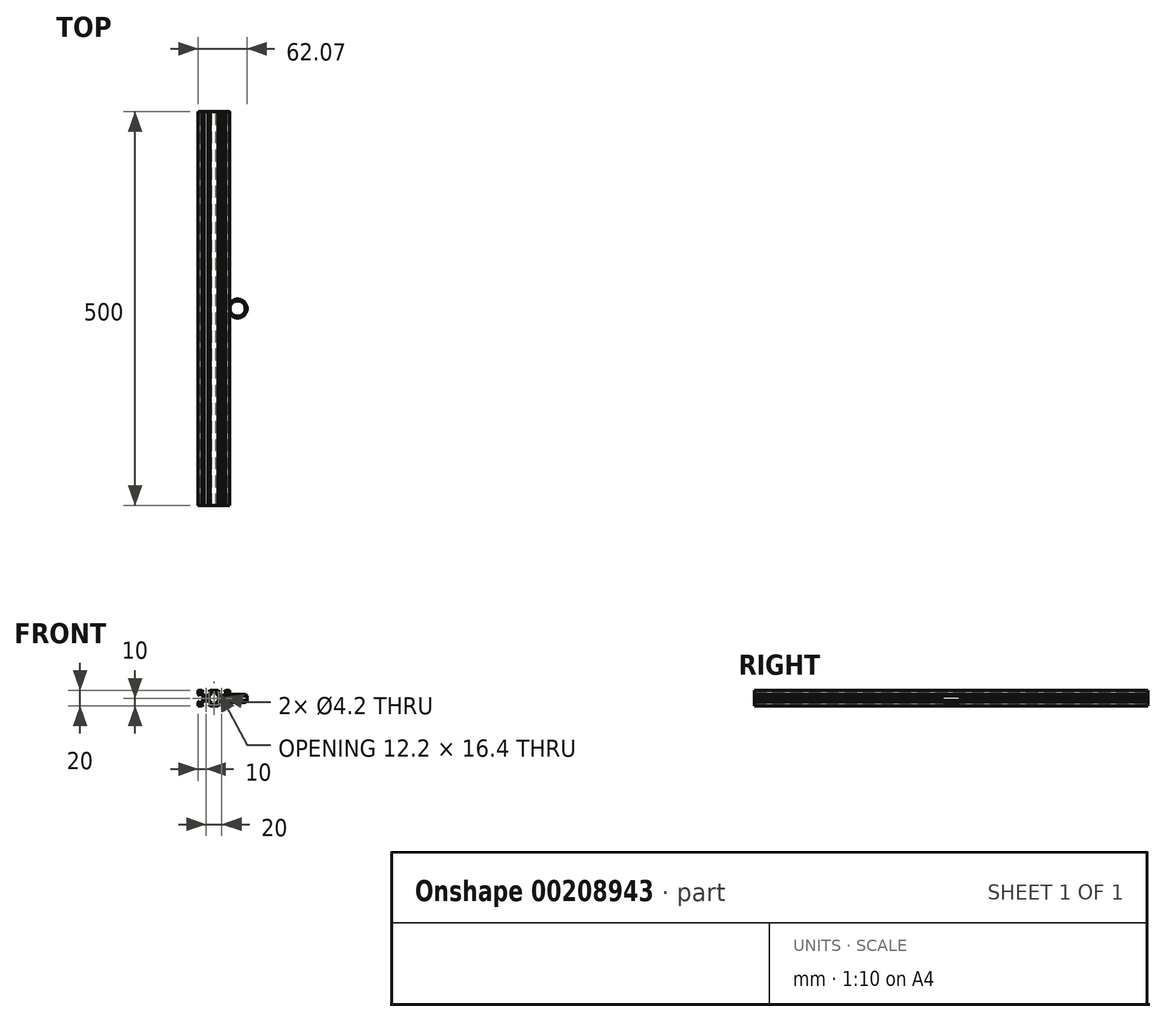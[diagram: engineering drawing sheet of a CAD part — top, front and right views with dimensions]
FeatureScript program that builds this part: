
annotation { "Feature Type Name" : "Feature", "Feature Type Description" : "" }
export const myFeature = defineFeature(function(context is Context, id is Id, definition is map)
    precondition{}
    {
        {
            var Q0;
            Q0=qCreatedBy(makeId("Front.planeOp"),FACE);
            var sketch = newSketch(context, id + "F0", { "sketchPlane" : qUnion([Q0])});
            skLineSegment(sketch, "E0", {"start": v(2.7, -8.2) * mm, "end": v(2.7, -6.24) * mm});
            skLineSegment(sketch, "E1", {"start": v(2.7, -6.24) * mm, "end": v(6.1, -2.84) * mm});
            skLineSegment(sketch, "E2", {"start": v(6.1, -2.84) * mm, "end": v(6.1, 2.84) * mm});
            skLineSegment(sketch, "E3", {"start": v(6.1, 2.84) * mm, "end": v(2.7, 6.24) * mm});
            skLineSegment(sketch, "E4", {"start": v(2.7, 6.24) * mm, "end": v(2.7, 8.2) * mm});
            skLineSegment(sketch, "E5", {"start": v(2.7, 8.2) * mm, "end": v(0, 8.2) * mm});
            skLineSegment(sketch, "E6", {"start": v(0, 8.2) * mm, "end": v(0, 0) * mm});
            skLineSegment(sketch, "E7", {"start": v(2.7, -8.2) * mm, "end": v(0, -8.2) * mm});
            skLineSegment(sketch, "E8", {"start": v(0, -8.2) * mm, "end": v(0, 0) * mm});
            skPoint(sketch, "E9.middle", {"position": v(0, 0) * mm});
            skLineSegment(sketch, "E10", {"start": v(5.07, 10) * mm, "end": v(0, 10) * mm});
            skLineSegment(sketch, "E11", {"start": v(0, 10) * mm, "end": v(0, 8.2) * mm});
            skLineSegment(sketch, "E12", {"start": v(0, -10) * mm, "end": v(0, -8.2) * mm});
            skPoint(sketch, "E13.endSnap0", {"position": v(6.1, 0) * mm});
            skLineSegment(sketch, "E14", {"start": v(0, -10) * mm, "end": v(5.07, -10) * mm});
            skCircle(sketch, "E15", {"center": v(10, 0) * mm, "radius": 2.1 * mm});
            skLineSegment(sketch, "E16", {"start": v(5.07, 10) * mm, "end": v(6.87, 8.2) * mm});
            skLineSegment(sketch, "E17", {"start": v(6.87, 8.2) * mm, "end": v(4.5, 8.2) * mm});
            skLineSegment(sketch, "E18", {"start": v(4.5, 8.2) * mm, "end": v(4.5, 6.56) * mm});
            skLineSegment(sketch, "E19", {"start": v(4.5, 6.56) * mm, "end": v(7.53, 3.53) * mm});
            skPoint(sketch, "E20.endSnap0", {"position": v(9.63, 5.16) * mm});
            skLineSegment(sketch, "E21", {"start": v(7.53, 3.53) * mm, "end": v(10, 3.53) * mm});
            skLineSegment(sketch, "E22.MirrorCS", {"start": v(12.47, 3.53) * mm, "end": v(10, 3.53) * mm});
            skLineSegment(sketch, "E23.MirrorCS", {"start": v(15.5, 6.56) * mm, "end": v(12.47, 3.53) * mm});
            skLineSegment(sketch, "E24.MirrorCS", {"start": v(15.5, 8.2) * mm, "end": v(15.5, 6.56) * mm});
            skLineSegment(sketch, "E25.MirrorCS", {"start": v(13.13, 8.2) * mm, "end": v(15.5, 8.2) * mm});
            skLineSegment(sketch, "E26.MirrorCS", {"start": v(14.93, 10) * mm, "end": v(13.13, 8.2) * mm});
            skLineSegment(sketch, "E27.MirrorCS", {"start": v(14.93, 10) * mm, "end": v(19.5, 10) * mm});
            skLineSegment(sketch, "E28.MirrorCS", {"start": v(20, 4.93) * mm, "end": v(18.2, 3.12) * mm});
            skLineSegment(sketch, "E29.MirrorCS", {"start": v(18.2, 5.5) * mm, "end": v(16.56, 5.5) * mm});
            skLineSegment(sketch, "E30.MirrorCS", {"start": v(16.56, 5.5) * mm, "end": v(13.53, 2.47) * mm});
            skLineSegment(sketch, "E31.MirrorCS", {"start": v(13.53, -2.47) * mm, "end": v(13.53, 0) * mm});
            skLineSegment(sketch, "E32.MirrorCS", {"start": v(13.53, 2.47) * mm, "end": v(13.53, 0) * mm});
            skLineSegment(sketch, "E33.MirrorCS", {"start": v(18.2, 3.12) * mm, "end": v(18.2, 5.5) * mm});
            skLineSegment(sketch, "E34.MirrorCS", {"start": v(16.56, -5.5) * mm, "end": v(13.53, -2.47) * mm});
            skLineSegment(sketch, "E35.MirrorCS", {"start": v(18.2, -5.5) * mm, "end": v(16.56, -5.5) * mm});
            skLineSegment(sketch, "E36.MirrorCS", {"start": v(18.2, -3.13) * mm, "end": v(18.2, -5.5) * mm});
            skLineSegment(sketch, "E37.MirrorCS", {"start": v(20, -4.93) * mm, "end": v(18.2, -3.12) * mm});
            skLineSegment(sketch, "E38", {"start": v(20, 9.5) * mm, "end": v(20, 4.93) * mm});
            skLineSegment(sketch, "E39.MirrorCS", {"start": v(20, -9.5) * mm, "end": v(20, -4.93) * mm});
            skLineSegment(sketch, "E40.MirrorCS", {"start": v(14.93, -10) * mm, "end": v(19.5, -10) * mm});
            skLineSegment(sketch, "E41.MirrorCS", {"start": v(14.93, -10) * mm, "end": v(13.13, -8.2) * mm});
            skLineSegment(sketch, "E42.MirrorCS", {"start": v(13.13, -8.2) * mm, "end": v(15.5, -8.2) * mm});
            skLineSegment(sketch, "E43.MirrorCS", {"start": v(15.5, -8.2) * mm, "end": v(15.5, -6.56) * mm});
            skLineSegment(sketch, "E44.MirrorCS", {"start": v(15.5, -6.56) * mm, "end": v(12.47, -3.53) * mm});
            skLineSegment(sketch, "E45.MirrorCS", {"start": v(12.47, -3.53) * mm, "end": v(10, -3.53) * mm});
            skLineSegment(sketch, "E46.MirrorCS", {"start": v(7.53, -3.53) * mm, "end": v(10, -3.53) * mm});
            skLineSegment(sketch, "E47.MirrorCS", {"start": v(4.5, -6.56) * mm, "end": v(7.53, -3.53) * mm});
            skLineSegment(sketch, "E48.MirrorCS", {"start": v(4.5, -8.2) * mm, "end": v(4.5, -6.56) * mm});
            skLineSegment(sketch, "E49.MirrorCS", {"start": v(6.87, -8.2) * mm, "end": v(4.5, -8.2) * mm});
            skLineSegment(sketch, "E50.MirrorCS", {"start": v(5.07, -10) * mm, "end": v(6.87, -8.2) * mm});
            skLineSegment(sketch, "E51.MirrorCS", {"start": v(-7.53, 3.53) * mm, "end": v(-10, 3.53) * mm});
            skCircle(sketch, "E52.MirrorC", {"center": v(-10, 0) * mm, "radius": 2.1 * mm});
            skLineSegment(sketch, "E53.MirrorCS", {"start": v(-6.1, -2.84) * mm, "end": v(-6.1, 2.84) * mm});
            skLineSegment(sketch, "E54.MirrorCS", {"start": v(-18.2, -3.13) * mm, "end": v(-18.2, -5.5) * mm});
            skLineSegment(sketch, "E55.MirrorCS", {"start": v(-14.93, 10) * mm, "end": v(-19.5, 10) * mm});
            skLineSegment(sketch, "E56.MirrorCS", {"start": v(0, -10) * mm, "end": v(-5.07, -10) * mm});
            skLineSegment(sketch, "E57.MirrorCS", {"start": v(-14.93, -10) * mm, "end": v(-13.13, -8.2) * mm});
            skLineSegment(sketch, "E58.MirrorCS", {"start": v(-14.93, 10) * mm, "end": v(-13.13, 8.2) * mm});
            skLineSegment(sketch, "E59.MirrorCS", {"start": v(-6.87, 8.2) * mm, "end": v(-4.5, 8.2) * mm});
            skLineSegment(sketch, "E60.MirrorCS", {"start": v(-20, -4.93) * mm, "end": v(-18.2, -3.12) * mm});
            skLineSegment(sketch, "E61.MirrorCS", {"start": v(-2.7, -8.2) * mm, "end": v(0, -8.2) * mm});
            skLineSegment(sketch, "E62.MirrorCS", {"start": v(-20, 4.93) * mm, "end": v(-18.2, 3.12) * mm});
            skLineSegment(sketch, "E63.MirrorCS", {"start": v(-2.7, -8.2) * mm, "end": v(-2.7, -6.24) * mm});
            skLineSegment(sketch, "E64.MirrorCS", {"start": v(-7.53, -3.53) * mm, "end": v(-10, -3.53) * mm});
            skLineSegment(sketch, "E65.MirrorCS", {"start": v(-13.13, -8.2) * mm, "end": v(-15.5, -8.2) * mm});
            skLineSegment(sketch, "E66.MirrorCS", {"start": v(-14.93, -10) * mm, "end": v(-19.5, -10) * mm});
            skLineSegment(sketch, "E67.MirrorCS", {"start": v(-6.87, -8.2) * mm, "end": v(-4.5, -8.2) * mm});
            skLineSegment(sketch, "E68.MirrorCS", {"start": v(-5.07, 10) * mm, "end": v(-6.87, 8.2) * mm});
            skLineSegment(sketch, "E69.MirrorCS", {"start": v(-13.53, 2.47) * mm, "end": v(-13.53, 0) * mm});
            skPoint(sketch, "E70.MirrorP", {"position": v(-6.1, 0) * mm});
            skLineSegment(sketch, "E71.MirrorCS", {"start": v(-15.5, -8.2) * mm, "end": v(-15.5, -6.56) * mm});
            skLineSegment(sketch, "E72.MirrorCS", {"start": v(-5.07, 10) * mm, "end": v(0, 10) * mm});
            skLineSegment(sketch, "E73.MirrorCS", {"start": v(-20, 9.5) * mm, "end": v(-20, 4.93) * mm});
            skLineSegment(sketch, "E74.MirrorCS", {"start": v(-18.2, 5.5) * mm, "end": v(-16.56, 5.5) * mm});
            skLineSegment(sketch, "E75.MirrorCS", {"start": v(-18.2, 3.12) * mm, "end": v(-18.2, 5.5) * mm});
            skLineSegment(sketch, "E76.MirrorCS", {"start": v(-15.5, 8.2) * mm, "end": v(-15.5, 6.56) * mm});
            skLineSegment(sketch, "E77.MirrorCS", {"start": v(-2.7, 6.24) * mm, "end": v(-2.7, 8.2) * mm});
            skLineSegment(sketch, "E78.MirrorCS", {"start": v(-16.56, 5.5) * mm, "end": v(-13.53, 2.47) * mm});
            skLineSegment(sketch, "E79.MirrorCS", {"start": v(-15.5, 6.56) * mm, "end": v(-12.47, 3.53) * mm});
            skLineSegment(sketch, "E80.MirrorCS", {"start": v(-16.56, -5.5) * mm, "end": v(-13.53, -2.47) * mm});
            skLineSegment(sketch, "E81.MirrorCS", {"start": v(-4.5, 6.56) * mm, "end": v(-7.53, 3.53) * mm});
            skLineSegment(sketch, "E82.MirrorCS", {"start": v(-20, -9.5) * mm, "end": v(-20, -4.93) * mm});
            skLineSegment(sketch, "E83.MirrorCS", {"start": v(-2.7, -6.24) * mm, "end": v(-6.1, -2.84) * mm});
            skLineSegment(sketch, "E84.MirrorCS", {"start": v(-4.5, 8.2) * mm, "end": v(-4.5, 6.56) * mm});
            skLineSegment(sketch, "E85.MirrorCS", {"start": v(-18.2, -5.5) * mm, "end": v(-16.56, -5.5) * mm});
            skLineSegment(sketch, "E86.MirrorCS", {"start": v(-4.5, -8.2) * mm, "end": v(-4.5, -6.56) * mm});
            skLineSegment(sketch, "E87.MirrorCS", {"start": v(-12.47, 3.53) * mm, "end": v(-10, 3.53) * mm});
            skLineSegment(sketch, "E88.MirrorCS", {"start": v(-13.53, -2.47) * mm, "end": v(-13.53, 0) * mm});
            skLineSegment(sketch, "E89.MirrorCS", {"start": v(-6.1, 2.84) * mm, "end": v(-2.7, 6.24) * mm});
            skLineSegment(sketch, "E90.MirrorCS", {"start": v(-15.5, -6.56) * mm, "end": v(-12.47, -3.53) * mm});
            skLineSegment(sketch, "E91.MirrorCS", {"start": v(-2.7, 8.2) * mm, "end": v(0, 8.2) * mm});
            skLineSegment(sketch, "E92.MirrorCS", {"start": v(-5.07, -10) * mm, "end": v(-6.87, -8.2) * mm});
            skLineSegment(sketch, "E93.MirrorCS", {"start": v(-4.5, -6.56) * mm, "end": v(-7.53, -3.53) * mm});
            skLineSegment(sketch, "E94.MirrorCS", {"start": v(-12.47, -3.53) * mm, "end": v(-10, -3.53) * mm});
            skLineSegment(sketch, "E95.MirrorCS", {"start": v(-13.13, 8.2) * mm, "end": v(-15.5, 8.2) * mm});
            skPoint(sketch, "E96.MirrorP", {"position": v(-9.63, 5.16) * mm});
            skPoint(sketch, "E97.visualSharp", {"position": v(20, 10) * mm});
            skArc(sketch, "E97.filletArc", {"start": v(20, 9.5) * mm, "mid": v(19.85, 9.85) * mm, "end": v(19.5, 10) * mm});
            skPoint(sketch, "E98.visualSharp", {"position": v(20, -10) * mm});
            skArc(sketch, "E98.filletArc", {"start": v(19.5, -10) * mm, "mid": v(19.85, -9.85) * mm, "end": v(20, -9.5) * mm});
            skPoint(sketch, "E99.visualSharp", {"position": v(-20, -10) * mm});
            skArc(sketch, "E99.filletArc", {"start": v(-20, -9.5) * mm, "mid": v(-19.85, -9.85) * mm, "end": v(-19.5, -10) * mm});
            skPoint(sketch, "E100.visualSharp", {"position": v(-20, 10) * mm});
            skArc(sketch, "E100.filletArc", {"start": v(-19.5, 10) * mm, "mid": v(-19.85, 9.85) * mm, "end": v(-20, 9.5) * mm});
            skSolve(sketch);
        }
        {
            var Q0;
            Q0=makeQuery(id+"F0.imprint","IMPRINT",FACE,{"disambiguationData":[TD([[makeQuery(id+"F0.imprint","IMPRINT",EDGE,{"derivedFrom":sQuery(id+"F0.wireOp",EDGE,"E0")}),-1.0]])]});
            var Q1;
            Q1=makeQuery(id+"F0.imprint","IMPRINT",FACE,{"disambiguationData":[TD([[makeQuery(id+"F0.imprint","IMPRINT",EDGE,{"derivedFrom":sQuery(id+"F0.wireOp",EDGE,"E11")}),-1.0]])]});
            extrude(context, id + "F1", {"entities" : qUnion([Q0, Q1]), "endBound" : BoundingType.SYMMETRIC, "depth" : 500 * mm});
        }
        {
            var Q0;
            Q0=qCreatedBy(makeId("Front.planeOp"),FACE);
            var sketch = newSketch(context, id + "F2", { "sketchPlane" : qUnion([Q0])});
            skPoint(sketch, "E101.middle", {"position": v(30.12, 0) * mm});
            skPoint(sketch, "E102.endSnap0", {"position": v(42.07, 0) * mm});
            skLineSegment(sketch, "E103", {"start": v(39.9, 5.12) * mm, "end": v(42.07, 2.94) * mm});
            skLineSegment(sketch, "E104.MirrorCS", {"start": v(39.9, -5.12) * mm, "end": v(42.07, -2.94) * mm});
            skLineSegment(sketch, "E105", {"start": v(30.12, 5.12) * mm, "end": v(30.12, -5.12) * mm});
            skLineSegment(sketch, "E106", {"start": v(30.12, 5.12) * mm, "end": v(39.9, 5.12) * mm});
            skLineSegment(sketch, "E107", {"start": v(39.9, -5.12) * mm, "end": v(30.12, -5.12) * mm});
            skLineSegment(sketch, "E108", {"start": v(42.07, 2.94) * mm, "end": v(42.07, -2.94) * mm});
            skSolve(sketch);
        }
        {
            var Q0;
            {var subQ0=sQuery(id+"F2.wireOp",EDGE,"E103");Q0=makeQuery(id+"F2.imprint","IMPRINT",FACE,{"disambiguationData":[TD([[makeQuery(id+"F2.imprint","IMPRINT",EDGE,{"derivedFrom":subQ0}),-1.0]])]});}
            var Q1;
            Q1=sQuery(id+"F2.wireOp",EDGE,"E105");
            revolve(context, id + "F3", {"entities" : qUnion([Q0]), "axis" : qUnion([Q1]), "revolveType" : RevolveType.FULL});
        }
    });
